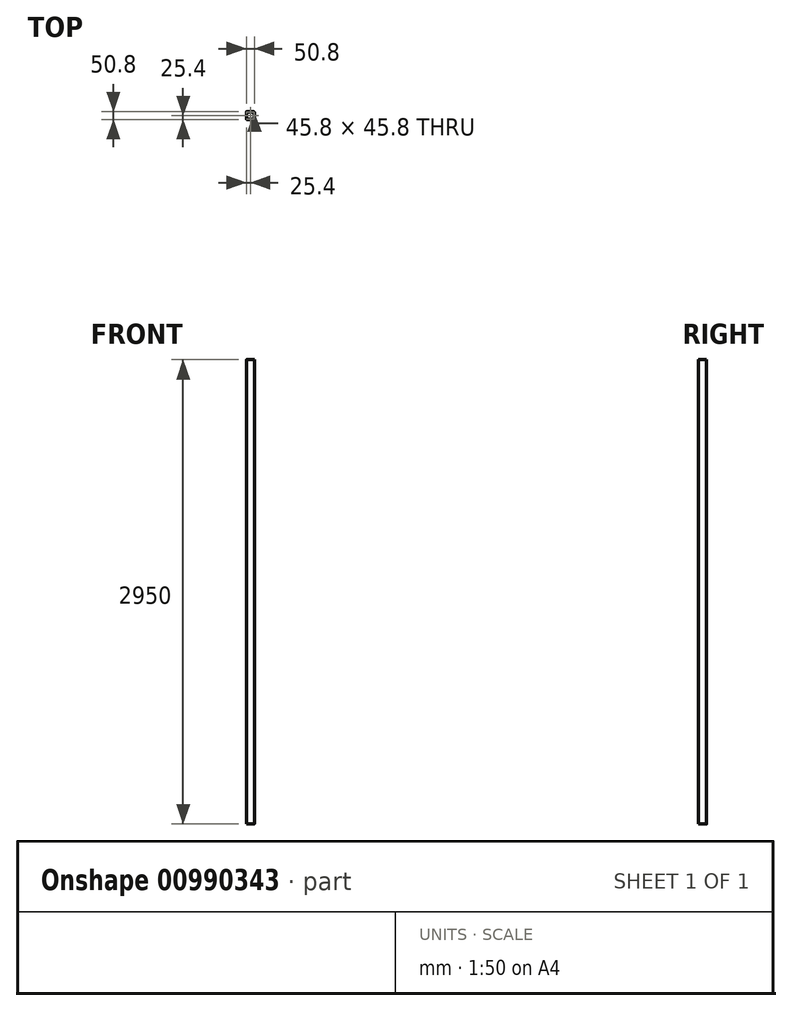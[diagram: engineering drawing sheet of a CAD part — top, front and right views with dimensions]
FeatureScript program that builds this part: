
annotation { "Feature Type Name" : "Feature", "Feature Type Description" : "" }
export const myFeature = defineFeature(function(context is Context, id is Id, definition is map)
    precondition{}
    {
        {
            var Q0;
            Q0=qCreatedBy(makeId("Top.planeOp"),FACE);
            var sketch = newSketch(context, id + "F0", { "sketchPlane" : qUnion([Q0])});
            skLineSegment(sketch, "E0.bottom", {"start": v(22.9, 25.4) * mm, "end": v(-22.9, 25.4) * mm});
            skLineSegment(sketch, "E0.top", {"start": v(22.9, -25.4) * mm, "end": v(-22.9, -25.4) * mm});
            skLineSegment(sketch, "E0.left", {"start": v(25.4, 22.9) * mm, "end": v(25.4, -22.9) * mm});
            skLineSegment(sketch, "E0.right", {"start": v(-25.4, 22.9) * mm, "end": v(-25.4, -22.9) * mm});
            skPoint(sketch, "E0.middle", {"position": v(0, 0) * mm});
            skPoint(sketch, "E1.visualSharp", {"position": v(25.4, 25.4) * mm});
            skArc(sketch, "E1.filletArc", {"start": v(25.4, 22.9) * mm, "mid": v(24.67, 24.67) * mm, "end": v(22.9, 25.4) * mm});
            skPoint(sketch, "E2.visualSharp", {"position": v(-25.4, 25.4) * mm});
            skArc(sketch, "E2.filletArc", {"start": v(-22.9, 25.4) * mm, "mid": v(-24.67, 24.67) * mm, "end": v(-25.4, 22.9) * mm});
            skPoint(sketch, "E3.visualSharp", {"position": v(-25.4, -25.4) * mm});
            skArc(sketch, "E3.filletArc", {"start": v(-25.4, -22.9) * mm, "mid": v(-24.67, -24.67) * mm, "end": v(-22.9, -25.4) * mm});
            skPoint(sketch, "E4.visualSharp", {"position": v(25.4, -25.4) * mm});
            skArc(sketch, "E4.filletArc", {"start": v(22.9, -25.4) * mm, "mid": v(24.67, -24.67) * mm, "end": v(25.4, -22.9) * mm});
            skLineSegment(sketch, "E5.0", {"start": v(22.9, 22.9) * mm, "end": v(22.9, 22.9) * mm});
            skLineSegment(sketch, "E5.1", {"start": v(22.9, 22.9) * mm, "end": v(22.9, -22.9) * mm});
            skLineSegment(sketch, "E5.2", {"start": v(22.9, 22.9) * mm, "end": v(-22.9, 22.9) * mm});
            skLineSegment(sketch, "E5.3", {"start": v(22.9, -22.9) * mm, "end": v(22.9, -22.9) * mm});
            skLineSegment(sketch, "E5.4", {"start": v(-22.9, 22.9) * mm, "end": v(-22.9, 22.9) * mm});
            skLineSegment(sketch, "E5.5", {"start": v(-22.9, 22.9) * mm, "end": v(-22.9, -22.9) * mm});
            skLineSegment(sketch, "E5.6", {"start": v(-22.9, -22.9) * mm, "end": v(-22.9, -22.9) * mm});
            skLineSegment(sketch, "E5.7", {"start": v(22.9, -22.9) * mm, "end": v(-22.9, -22.9) * mm});
            skSolve(sketch);
        }
        {
            var Q0;
            Q0=makeQuery(id+"F0.imprint","IMPRINT",FACE,{"disambiguationData":[TD([[makeQuery(id+"F0.imprint","IMPRINT",EDGE,{"derivedFrom":sQuery(id+"F0.wireOp",EDGE,"E0.bottom")}),1.0]])]});
            extrude(context, id + "F1", {"entities" : qUnion([Q0]), "depth" : 2950 * mm, "offsetDistance" : 25 * mm});
        }
    });
